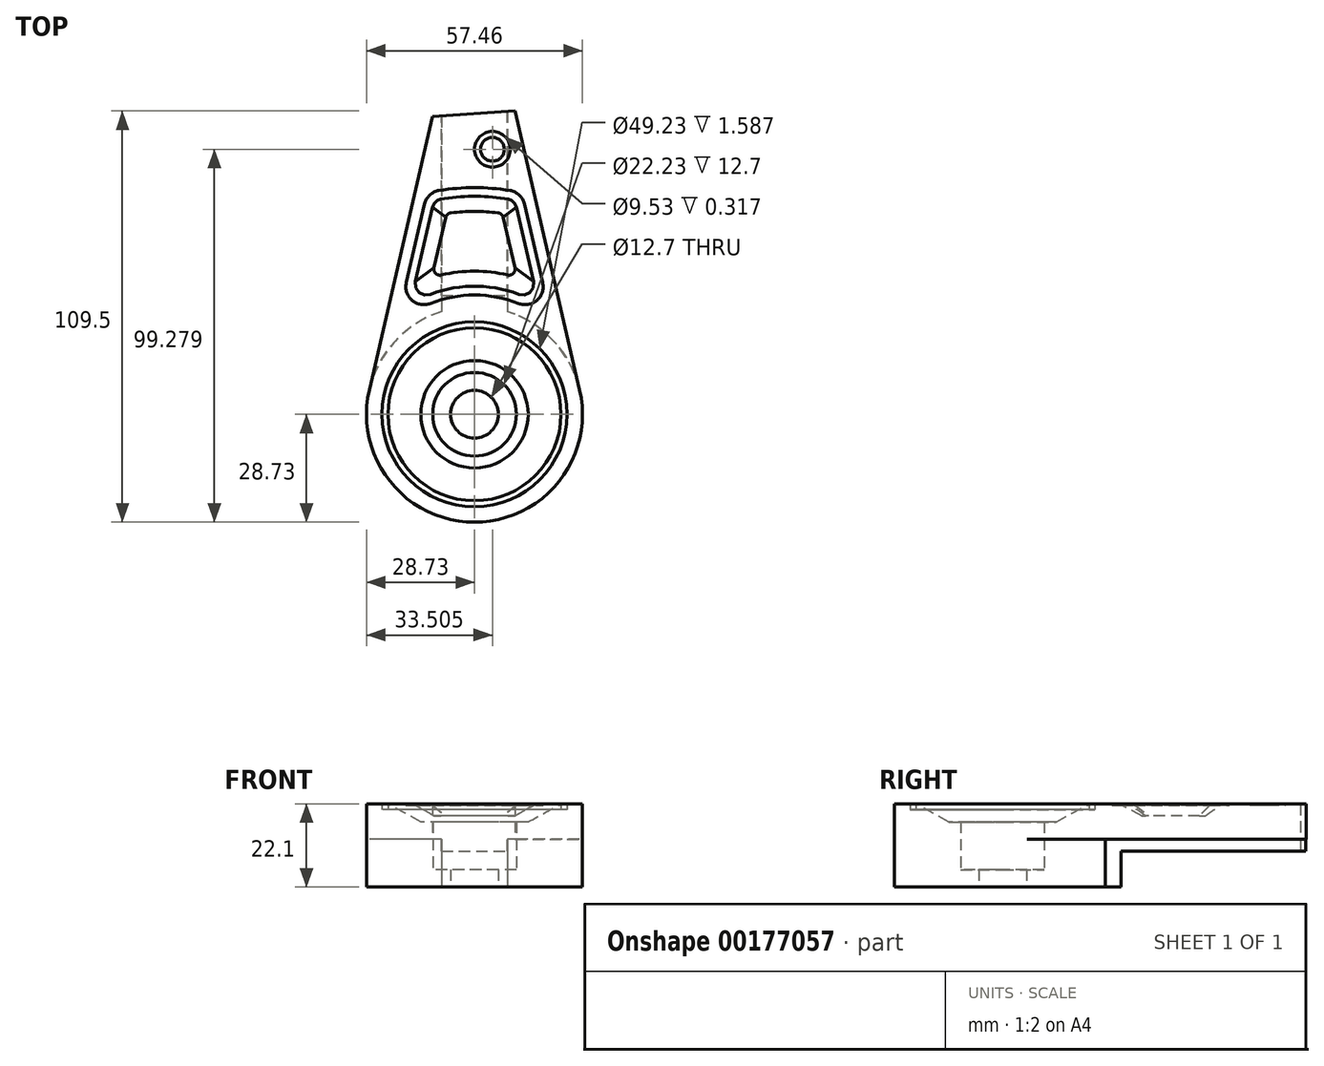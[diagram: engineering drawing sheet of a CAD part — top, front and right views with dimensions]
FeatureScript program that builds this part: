
annotation { "Feature Type Name" : "Feature", "Feature Type Description" : "" }
export const myFeature = defineFeature(function(context is Context, id is Id, definition is map)
    precondition{}
    {
        {
            var Q0;
            Q0=qCreatedBy(makeId("Top.planeOp"),FACE);
            var sketch = newSketch(context, id + "F0", { "sketchPlane" : qUnion([Q0])});
            skArc(sketch, "E0", {"start": v(-8.74, 27.37) * mm, "mid": v(0, -28.73) * mm, "end": v(8.74, 27.37) * mm});
            skLineSegment(sketch, "E1.bottom", {"start": v(-8.74, 31.6) * mm, "end": v(8.74, 31.6) * mm});
            skLineSegment(sketch, "E1.left", {"start": v(-8.74, 31.6) * mm, "end": v(-8.74, 27.37) * mm});
            skLineSegment(sketch, "E1.right", {"start": v(8.74, 31.6) * mm, "end": v(8.74, 27.37) * mm});
            skSolve(sketch);
        }
        {
            var Q0;
            Q0 = qSketchRegion(id + "F0", true);
            extrude(context, id + "F1", {"entities" : qUnion([Q0]), "depth" : 12.7 * mm});
        }
        {
            var Q0;
            Q0=makeQuery(id+"F1.opExtrude","CAP_FACE",FACE,{"disambiguationData":[OSD([sQuery(id+"F0.wireOp",EDGE,"E0"),sQuery(id+"F0.wireOp",EDGE,"E1.bottom"),sQuery(id+"F0.wireOp",EDGE,"E1.left"),sQuery(id+"F0.wireOp",EDGE,"E1.right")])],"isStart":false});
            var sketch = newSketch(context, id + "F2", { "sketchPlane" : qUnion([Q0])});
            skArc(sketch, "E2", {"start": v(-28, 6.46) * mm, "mid": v(0, -28.73) * mm, "end": v(28, 6.46) * mm});
            skLineSegment(sketch, "E3", {"start": v(10.84, 80.77) * mm, "end": v(-11.2, 79.23) * mm});
            skPoint(sketch, "E4.orphan", {"position": v(-37.72, -35.67) * mm});
            skPoint(sketch, "E5.orphan", {"position": v(37.72, -35.67) * mm});
            skLineSegment(sketch, "E6.trimOffspring", {"start": v(-11.2, 79.23) * mm, "end": v(-28, 6.46) * mm});
            skLineSegment(sketch, "E7.trimOffspring", {"start": v(10.84, 80.77) * mm, "end": v(28, 6.46) * mm});
            skPoint(sketch, "E8.MirrorCS.start.orphan", {"position": v(-27.86, 248.39) * mm});
            skPoint(sketch, "E9.start.orphan", {"position": v(27.86, 248.39) * mm});
            skSolve(sketch);
        }
        {
            var Q0;
            Q0 = qSketchRegion(id + "F2", true);
            extrude(context, id + "F3", {"entities" : qUnion([Q0]), "operationType" : NewBodyOperationType.ADD, "depth" : 9.4 * mm});
        }
        {
            var Q0;
            Q0=makeQuery(id+"F3.opExtrude","CAP_FACE",FACE,{"disambiguationData":[OSD([sQuery(id+"F2.wireOp",EDGE,"E2"),sQuery(id+"F2.wireOp",EDGE,"E3"),sQuery(id+"F2.wireOp",EDGE,"E6.trimOffspring"),sQuery(id+"F2.wireOp",EDGE,"E7.trimOffspring")])],"isStart":true});
            var sketch = newSketch(context, id + "F4", { "sketchPlane" : qUnion([Q0])});
            skLineSegment(sketch, "E10.bottom", {"start": v(8.74, -31.6) * mm, "end": v(-8.74, -31.6) * mm});
            skLineSegment(sketch, "E10.left", {"start": v(8.74, -31.6) * mm, "end": v(8.74, -80.63) * mm});
            skLineSegment(sketch, "E10.right", {"start": v(-8.74, -31.6) * mm, "end": v(-8.74, -79.4) * mm});
            skLineSegment(sketch, "E11", {"start": v(8.74, -80.63) * mm, "end": v(-8.74, -79.4) * mm});
            skSolve(sketch);
        }
        {
            var Q0;
            Q0=makeQuery(id+"F4.imprint","IMPRINT",FACE,{"disambiguationData":[TD([[makeQuery(id+"F4.imprint","IMPRINT",EDGE,{"derivedFrom":sQuery(id+"F4.wireOp",EDGE,"E10.bottom")}),-1.0]])]});
            var Q1;
            Q1 = qConstructionFilter(qBodyType(qCreatedBy(id + "F4" ,EDGE), BodyType.WIRE), ConstructionObject.NO);
            extrude(context, id + "F5", {"entities" : qUnion([Q0]), "operationType" : NewBodyOperationType.ADD, "surfaceEntities" : qUnion([Q1]), "depth" : 3.17 * mm});
        }
        {
            var Q0;
            Q0=makeQuery(id+"F3.opExtrude","CAP_FACE",FACE,{"disambiguationData":[OSD([sQuery(id+"F2.wireOp",EDGE,"E2"),sQuery(id+"F2.wireOp",EDGE,"E3"),sQuery(id+"F2.wireOp",EDGE,"E6.trimOffspring"),sQuery(id+"F2.wireOp",EDGE,"E7.trimOffspring")])],"isStart":false});
            var sketch = newSketch(context, id + "F6", { "sketchPlane" : qUnion([Q0])});
            skCircle(sketch, "E12", {"center": v(0, 0) * mm, "radius": 24.61 * mm});
            skCircle(sketch, "E13", {"center": v(0, 0) * mm, "radius": 23.03 * mm});
            skSolve(sketch);
        }
        {
            var Q0;
            Q0 = qSketchRegion(id + "F6", true);
            extrude(context, id + "F7", {"entities" : qUnion([Q0]), "endBound" : BoundingType.SYMMETRIC, "depth" : 3.17 * mm});
        }
        {
            var Q0;
            Q0=makeQuery(id+"F7.opExtrude","SWEPT_BODY",BODY,{"disambiguationData":[OSD([sQuery(id+"F6.wireOp",EDGE,"E12"),sQuery(id+"F6.wireOp",EDGE,"E13")])]});
            var Q1;
            Q1=makeQuery(id+"F1.opExtrude","SWEPT_BODY",BODY,{"disambiguationData":[OSD([sQuery(id+"F0.wireOp",EDGE,"E0"),sQuery(id+"F0.wireOp",EDGE,"E1.bottom"),sQuery(id+"F0.wireOp",EDGE,"E1.left"),sQuery(id+"F0.wireOp",EDGE,"E1.right")])]});
            booleanBodies(context, id + "F8", {"operationType" : BooleanOperationType.SUBTRACTION, "tools" : qUnion([Q0]), "targets" : qUnion([Q1])});
        }
        {
            var Q0;
            Q0=qCreatedBy(makeId("Front.planeOp"),FACE);
            var sketch = newSketch(context, id + "F9", { "sketchPlane" : qUnion([Q0])});
            skLineSegment(sketch, "E14.bottom", {"start": v(0, 22.1) * mm, "end": v(14.29, 22.1) * mm});
            skLineSegment(sketch, "E14.top", {"start": v(0, 17.32) * mm, "end": v(14.29, 17.32) * mm});
            skLineSegment(sketch, "E14.left", {"start": v(0, 22.1) * mm, "end": v(0, 17.32) * mm});
            skLineSegment(sketch, "E15.bottom", {"start": v(0, 22.1) * mm, "end": v(23.03, 22.1) * mm});
            skLineSegment(sketch, "E15.left", {"start": v(0, 22.1) * mm, "end": v(0, 15.75) * mm});
            skLineSegment(sketch, "E16", {"start": v(23.03, 22.1) * mm, "end": v(14.29, 17.32) * mm});
            skSolve(sketch);
        }
        {
            var Q0;
            Q0 = qSketchRegion(id + "F9", true);
            var Q1;
            Q1=sQuery(id+"F9.wireOp",EDGE,"E15.left");
            revolve(context, id + "F10", {"entities" : qUnion([Q0]), "axis" : qUnion([Q1]), "revolveType" : RevolveType.FULL});
        }
        {
            var Q0;
            Q0=makeQuery(id+"F10.opRevolve","SWEPT_BODY",BODY,{"disambiguationData":[OSD([sQuery(id+"F9.wireOp",EDGE,"E14.top"),sQuery(id+"F9.wireOp",EDGE,"E15.bottom"),sQuery(id+"F9.wireOp",EDGE,"E15.left"),sQuery(id+"F9.wireOp",EDGE,"E16")])]});
            var Q1;
            Q1=makeQuery(id+"F1.opExtrude","SWEPT_BODY",BODY,{"disambiguationData":[OSD([sQuery(id+"F0.wireOp",EDGE,"E0"),sQuery(id+"F0.wireOp",EDGE,"E1.bottom"),sQuery(id+"F0.wireOp",EDGE,"E1.left"),sQuery(id+"F0.wireOp",EDGE,"E1.right")])]});
            booleanBodies(context, id + "F11", {"operationType" : BooleanOperationType.SUBTRACTION, "tools" : qUnion([Q0]), "targets" : qUnion([Q1])});
        }
        {
            var Q0;
            Q0=makeQuery(id+"F11.opBoolean","COPY",FACE,{"derivedFrom":makeQuery(id+"F10.opRevolve","SWEPT_FACE",FACE,{"disambiguationData":[OSD([sQuery(id+"F9.wireOp",EDGE,"E14.top")])]})});
            var sketch = newSketch(context, id + "F12", { "sketchPlane" : qUnion([Q0])});
            skCircle(sketch, "E17", {"center": v(0, 0) * mm, "radius": 11.11 * mm});
            skSolve(sketch);
        }
        {
            var Q0;
            Q0=makeQuery(id+"F12.imprint","IMPRINT",FACE,{"disambiguationData":[TD([[makeQuery(id+"F12.imprint","IMPRINT",EDGE,{"derivedFrom":sQuery(id+"F12.wireOp",EDGE,"E17")}),1.0]])]});
            extrude(context, id + "F13", {"entities" : qUnion([Q0]), "endBound" : BoundingType.SYMMETRIC, "depth" : 25.4 * mm});
        }
        {
            var Q0;
            Q0=makeQuery(id+"F13.opExtrude","SWEPT_BODY",BODY,{"disambiguationData":[OSD([sQuery(id+"F12.wireOp",EDGE,"E17")])]});
            var Q1;
            Q1=makeQuery(id+"F1.opExtrude","SWEPT_BODY",BODY,{"disambiguationData":[OSD([sQuery(id+"F0.wireOp",EDGE,"E0"),sQuery(id+"F0.wireOp",EDGE,"E1.bottom"),sQuery(id+"F0.wireOp",EDGE,"E1.left"),sQuery(id+"F0.wireOp",EDGE,"E1.right")])]});
            booleanBodies(context, id + "F14", {"operationType" : BooleanOperationType.SUBTRACTION, "tools" : qUnion([Q0]), "targets" : qUnion([Q1])});
        }
        {
            var Q0;
            {var subQ0=sQuery(id+"F2.wireOp",EDGE,"E6.trimOffspring");var subQ1=sQuery(id+"F2.wireOp",EDGE,"E3");var subQ2=sQuery(id+"F2.wireOp",EDGE,"E2");var subQ3=sQuery(id+"F2.wireOp",EDGE,"E7.trimOffspring");Q0=makeQuery(id+"F8.opBoolean","SPLIT",FACE,{"disambiguationData":[TD([makeQuery(id+"F1.opExtrude","SWEPT_FACE",FACE,{"disambiguationData":[OSD([sQuery(id+"F0.wireOp",EDGE,"E0")])]})])],"derivedFrom":makeQuery(id+"F3.opExtrude","CAP_FACE",FACE,{"disambiguationData":[OSD([subQ2,subQ1,subQ0,subQ3])],"isStart":false})});}
            var sketch = newSketch(context, id + "F15", { "sketchPlane" : qUnion([Q0])});
            skCircle(sketch, "E18", {"center": v(4.78, 70.55) * mm, "radius": 4.76 * mm});
            skCircle(sketch, "E19", {"center": v(4.78, 70.55) * mm, "radius": 3.18 * mm});
            skSolve(sketch);
        }
        {
            var Q0;
            Q0 = qSketchRegion(id + "F15", true);
            extrude(context, id + "F16", {"entities" : qUnion([Q0]), "endBound" : BoundingType.SYMMETRIC, "depth" : 0.64 * mm});
        }
        {
            var Q0;
            Q0=makeQuery(id+"F16.opExtrude","SWEPT_BODY",BODY,{"disambiguationData":[OSD([sQuery(id+"F15.wireOp",EDGE,"E18"),sQuery(id+"F15.wireOp",EDGE,"E19")])]});
            var Q1;
            Q1=makeQuery(id+"F1.opExtrude","SWEPT_BODY",BODY,{"disambiguationData":[OSD([sQuery(id+"F0.wireOp",EDGE,"E0"),sQuery(id+"F0.wireOp",EDGE,"E1.bottom"),sQuery(id+"F0.wireOp",EDGE,"E1.left"),sQuery(id+"F0.wireOp",EDGE,"E1.right")])]});
            booleanBodies(context, id + "F17", {"operationType" : BooleanOperationType.SUBTRACTION, "tools" : qUnion([Q0]), "targets" : qUnion([Q1])});
        }
        {
            var Q0;
            {var subQ0=sQuery(id+"F2.wireOp",EDGE,"E6.trimOffspring");var subQ2=sQuery(id+"F2.wireOp",EDGE,"E3");var subQ4=sQuery(id+"F2.wireOp",EDGE,"E2");var subQ6=makeQuery(id+"F1.opExtrude","SWEPT_FACE",FACE,{"disambiguationData":[OSD([sQuery(id+"F0.wireOp",EDGE,"E0")])]});var subQ7=sQuery(id+"F2.wireOp",EDGE,"E7.trimOffspring");Q0=makeQuery(id+"F17.opBoolean","SPLIT",FACE,{"disambiguationData":[TD([subQ6])],"derivedFrom":makeQuery(id+"F8.opBoolean","SPLIT",FACE,{"disambiguationData":[TD([subQ6])],"derivedFrom":makeQuery(id+"F3.opExtrude","CAP_FACE",FACE,{"disambiguationData":[OSD([subQ4,subQ2,subQ0,subQ7])],"isStart":false})})});}
            var sketch = newSketch(context, id + "F18", { "sketchPlane" : qUnion([Q0])});
            skArc(sketch, "E20", {"start": v(9.36, 59.6) * mm, "mid": v(0, 60.33) * mm, "end": v(-9.36, 59.6) * mm});
            skArc(sketch, "E21", {"start": v(11.72, 29.5) * mm, "mid": v(0, 31.75) * mm, "end": v(-11.72, 29.5) * mm});
            skLineSegment(sketch, "E22", {"start": v(18.14, 35.02) * mm, "end": v(13.32, 55.91) * mm});
            skLineSegment(sketch, "E23.MirrorCS", {"start": v(-18.14, 35.02) * mm, "end": v(-13.32, 55.91) * mm});
            skPoint(sketch, "E24.visualSharp", {"position": v(-11.28, 57.66) * mm});
            skPoint(sketch, "E25.visualSharp", {"position": v(11.28, 57.66) * mm});
            skPoint(sketch, "E26.visualSharp", {"position": v(-12.6, 59) * mm});
            skArc(sketch, "E26.filletArc", {"start": v(-9.36, 59.6) * mm, "mid": v(-11.9, 58.36) * mm, "end": v(-13.32, 55.91) * mm});
            skPoint(sketch, "E27.visualSharp", {"position": v(12.6, 59) * mm});
            skArc(sketch, "E27.filletArc", {"start": v(13.32, 55.91) * mm, "mid": v(11.9, 58.36) * mm, "end": v(9.36, 59.6) * mm});
            skPoint(sketch, "E28.visualSharp", {"position": v(-18.13, 27.99) * mm});
            skPoint(sketch, "E29.visualSharp", {"position": v(18.13, 27.99) * mm});
            skPoint(sketch, "E30.visualSharp", {"position": v(-20.66, 24.11) * mm});
            skArc(sketch, "E30.filletArc", {"start": v(-18.14, 35.02) * mm, "mid": v(-16.6, 30.32) * mm, "end": v(-11.72, 29.5) * mm});
            skPoint(sketch, "E31.visualSharp", {"position": v(20.66, 24.11) * mm});
            skArc(sketch, "E31.filletArc", {"start": v(11.72, 29.5) * mm, "mid": v(16.6, 30.32) * mm, "end": v(18.14, 35.02) * mm});
            skSolve(sketch);
        }
        {
            var Q0;
            Q0 = qSketchRegion(id + "F18", true);
            extrude(context, id + "F19", {"entities" : qUnion([Q0]), "endBound" : BoundingType.SYMMETRIC, "depth" : 0.76 * mm});
        }
        {
            var Q0;
            Q0=makeQuery(id+"F19.opExtrude","SWEPT_BODY",BODY,{"disambiguationData":[OSD([sQuery(id+"F18.wireOp",EDGE,"E20"),sQuery(id+"F18.wireOp",EDGE,"QQfPZb6T-z4vG-od9X-flIt-BDM9YzBF81dE"),sQuery(id+"F18.wireOp",EDGE,"E21"),sQuery(id+"F18.wireOp",EDGE,"x9Glj3Va-BeVH-0q31-jCwU-7eNUVLCWfRpr"),sQuery(id+"F18.wireOp",EDGE,"E22"),sQuery(id+"F18.wireOp",EDGE,"5VmBpSvH-0JUU-8XrI-SHU1-adJSwn0DBkaH"),sQuery(id+"F18.wireOp",EDGE,"E23.MirrorCS"),sQuery(id+"F18.wireOp",EDGE,"3f89a360-dbe8-4113-bc30-97e3e043b985.trimOffspring"),sQuery(id+"F18.wireOp",EDGE,"E24.filletArc"),sQuery(id+"F18.wireOp",EDGE,"E25.filletArc"),sQuery(id+"F18.wireOp",EDGE,"E26.filletArc"),sQuery(id+"F18.wireOp",EDGE,"E27.filletArc"),sQuery(id+"F18.wireOp",EDGE,"E28.filletArc"),sQuery(id+"F18.wireOp",EDGE,"E29.filletArc"),sQuery(id+"F18.wireOp",EDGE,"E30.filletArc"),sQuery(id+"F18.wireOp",EDGE,"E31.filletArc")])]});
            var Q1;
            Q1=makeQuery(id+"F1.opExtrude","SWEPT_BODY",BODY,{"disambiguationData":[OSD([sQuery(id+"F0.wireOp",EDGE,"E0"),sQuery(id+"F0.wireOp",EDGE,"E1.bottom"),sQuery(id+"F0.wireOp",EDGE,"E1.left"),sQuery(id+"F0.wireOp",EDGE,"E1.right")])]});
            booleanBodies(context, id + "F20", {"operationType" : BooleanOperationType.SUBTRACTION, "tools" : qUnion([Q0]), "targets" : qUnion([Q1])});
        }
        {
            var Q0;
            {var subQ0=sQuery(id+"F2.wireOp",EDGE,"E6.trimOffspring");var subQ2=sQuery(id+"F2.wireOp",EDGE,"E3");var subQ4=sQuery(id+"F2.wireOp",EDGE,"E2");var subQ6=makeQuery(id+"F1.opExtrude","SWEPT_FACE",FACE,{"disambiguationData":[OSD([sQuery(id+"F0.wireOp",EDGE,"E0")])]});var subQ7=sQuery(id+"F2.wireOp",EDGE,"E7.trimOffspring");Q0=makeQuery(id+"F17.opBoolean","SPLIT",FACE,{"disambiguationData":[TD([subQ6])],"derivedFrom":makeQuery(id+"F8.opBoolean","SPLIT",FACE,{"disambiguationData":[TD([subQ6])],"derivedFrom":makeQuery(id+"F3.opExtrude","CAP_FACE",FACE,{"disambiguationData":[OSD([subQ4,subQ2,subQ0,subQ7])],"isStart":false})})});}
            var sketch = newSketch(context, id + "F21", { "sketchPlane" : qUnion([Q0])});
            skLineSegment(sketch, "E32", {"start": v(10.74, 38.95) * mm, "end": v(7.63, 52.42) * mm});
            skArc(sketch, "E33", {"start": v(8.84, 37.06) * mm, "mid": v(0, 38.1) * mm, "end": v(-8.84, 37.06) * mm});
            skArc(sketch, "E34", {"start": v(6.28, 53.63) * mm, "mid": v(0, 54) * mm, "end": v(-6.28, 53.63) * mm});
            skLineSegment(sketch, "E35", {"start": v(-7.63, 52.42) * mm, "end": v(-10.74, 38.95) * mm});
            skPoint(sketch, "E36.visualSharp", {"position": v(-11.34, 36.37) * mm});
            skArc(sketch, "E36.filletArc", {"start": v(-10.74, 38.95) * mm, "mid": v(-10.32, 37.47) * mm, "end": v(-8.84, 37.06) * mm});
            skPoint(sketch, "E37.visualSharp", {"position": v(11.34, 36.37) * mm});
            skArc(sketch, "E37.filletArc", {"start": v(8.84, 37.06) * mm, "mid": v(10.32, 37.47) * mm, "end": v(10.74, 38.95) * mm});
            skPoint(sketch, "E38.visualSharp", {"position": v(7.38, 53.5) * mm});
            skArc(sketch, "E38.filletArc", {"start": v(7.63, 52.42) * mm, "mid": v(7.15, 53.24) * mm, "end": v(6.28, 53.63) * mm});
            skPoint(sketch, "E39.visualSharp", {"position": v(-7.38, 53.5) * mm});
            skArc(sketch, "E39.filletArc", {"start": v(-6.28, 53.63) * mm, "mid": v(-7.15, 53.24) * mm, "end": v(-7.63, 52.42) * mm});
            skSolve(sketch);
        }
        {
            var Q0;
            Q0=qCreatedBy(makeId("Top.planeOp"),FACE);
            cPlane(context, id + "F22", {"entities" : qUnion([Q0]), "cplaneType" : CPlaneType.OFFSET, "offset" : 25.4 * mm, "width" : 152.4 * mm, "height" : 152.4 * mm});
        }
        {
            var Q0;
            Q0=qCreatedBy(id+"F22.planeOp",FACE);
            var sketch = newSketch(context, id + "F23", { "sketchPlane" : qUnion([Q0])});
            skArc(sketch, "E40", {"start": v(9.17, 58.03) * mm, "mid": v(0, 58.75) * mm, "end": v(-9.17, 58.03) * mm});
            skArc(sketch, "E41", {"start": v(12.34, 30.98) * mm, "mid": v(0, 33.35) * mm, "end": v(-12.34, 30.98) * mm});
            skLineSegment(sketch, "E42", {"start": v(-16.6, 34.65) * mm, "end": v(-11.77, 55.6) * mm});
            skLineSegment(sketch, "E43", {"start": v(16.6, 34.65) * mm, "end": v(11.77, 55.6) * mm});
            skPoint(sketch, "E44.visualSharp", {"position": v(-11.3, 57.65) * mm});
            skArc(sketch, "E44.filletArc", {"start": v(-9.17, 58.03) * mm, "mid": v(-10.84, 57.22) * mm, "end": v(-11.77, 55.6) * mm});
            skPoint(sketch, "E45.visualSharp", {"position": v(-18.15, 27.98) * mm});
            skArc(sketch, "E45.filletArc", {"start": v(-16.6, 34.65) * mm, "mid": v(-15.58, 31.52) * mm, "end": v(-12.34, 30.98) * mm});
            skPoint(sketch, "E46.visualSharp", {"position": v(18.15, 27.98) * mm});
            skArc(sketch, "E46.filletArc", {"start": v(12.34, 30.98) * mm, "mid": v(15.58, 31.52) * mm, "end": v(16.6, 34.65) * mm});
            skPoint(sketch, "E47.visualSharp", {"position": v(11.3, 57.65) * mm});
            skArc(sketch, "E47.filletArc", {"start": v(11.77, 55.6) * mm, "mid": v(10.84, 57.22) * mm, "end": v(9.17, 58.03) * mm});
            skSolve(sketch);
        }
        {
            var Q0;
            Q0=makeQuery(id+"F1.opExtrude","CAP_FACE",FACE,{"disambiguationData":[OSD([sQuery(id+"F0.wireOp",EDGE,"E0"),sQuery(id+"F0.wireOp",EDGE,"E1.bottom"),sQuery(id+"F0.wireOp",EDGE,"E1.left"),sQuery(id+"F0.wireOp",EDGE,"E1.right")])],"isStart":true});
            var sketch = newSketch(context, id + "F24", { "sketchPlane" : qUnion([Q0])});
            skPoint(sketch, "E48", {"position": v(0, 0) * mm});
            skSolve(sketch);
        }
        {
            var Q0;
            Q0=sQuery(id+"F24.wireOp",VERTEX,"E48");
            var Q1;
            Q1=makeQuery(id+"F1.opExtrude","SWEPT_BODY",BODY,{"disambiguationData":[OSD([sQuery(id+"F0.wireOp",EDGE,"E0"),sQuery(id+"F0.wireOp",EDGE,"E1.bottom"),sQuery(id+"F0.wireOp",EDGE,"E1.left"),sQuery(id+"F0.wireOp",EDGE,"E1.right")])]});
            hole(context, id + "F25", {"style" : HoleStyle.SIMPLE, "endStyle" : HoleEndStyle.THROUGH, "holeDiameter" : 12.7 * mm, "startFromSketch" : true, "locations" : qUnion([Q0]), "scope" : qUnion([Q1]), "isTappedThrough" : true});
        }
        {
            var Q0;
            Q0=makeQuery(id+"F23.imprint","IMPRINT",FACE,{"disambiguationData":[TD([[makeQuery(id+"F23.imprint","IMPRINT",EDGE,{"derivedFrom":sQuery(id+"F23.wireOp",EDGE,"E40")}),1.0]])]});
            var Q1;
            Q1=makeQuery(id+"F21.imprint","IMPRINT",FACE,{"disambiguationData":[TD([[makeQuery(id+"F21.imprint","IMPRINT",EDGE,{"derivedFrom":sQuery(id+"F21.wireOp",EDGE,"E32")}),1.0]])]});
            loft(context, id + "F26", {"sheetProfilesArray" : [{ "sheetProfileEntities" : qUnion([Q0]) }, { "sheetProfileEntities" : qUnion([Q1]) }]});
        }
        {
            var Q0;
            Q0=makeQuery(id+"F26.opLoft","SWEPT_BODY",BODY,{"disambiguationData":[OSD([makeQuery(id+"F21.imprint","IMPRINT",FACE,{"disambiguationData":[TD([[makeQuery(id+"F21.imprint","IMPRINT",EDGE,{"derivedFrom":sQuery(id+"F21.wireOp",EDGE,"E32")}),1.0]])]}),makeQuery(id+"F23.imprint","IMPRINT",FACE,{"disambiguationData":[TD([[makeQuery(id+"F23.imprint","IMPRINT",EDGE,{"derivedFrom":sQuery(id+"F23.wireOp",EDGE,"E40")}),1.0]])]})])]});
            transform(context, id + "F27", {"entities" : qUnion([Q0]), "transformType" : TransformType.TRANSLATION_3D, "dx" : 0 * mm, "dy" : 0 * mm, "dz" : -3.17 * mm, "makeCopy" : false});
        }
        {
            var Q0;
            Q0=makeQuery(id+"F26.opLoft","SWEPT_BODY",BODY,{"disambiguationData":[OSD([makeQuery(id+"F21.imprint","IMPRINT",FACE,{"disambiguationData":[TD([[makeQuery(id+"F21.imprint","IMPRINT",EDGE,{"derivedFrom":sQuery(id+"F21.wireOp",EDGE,"E32")}),1.0]])]}),makeQuery(id+"F23.imprint","IMPRINT",FACE,{"disambiguationData":[TD([[makeQuery(id+"F23.imprint","IMPRINT",EDGE,{"derivedFrom":sQuery(id+"F23.wireOp",EDGE,"E40")}),1.0]])]})])]});
            var Q1;
            Q1=makeQuery(id+"F1.opExtrude","SWEPT_BODY",BODY,{"disambiguationData":[OSD([sQuery(id+"F0.wireOp",EDGE,"E0"),sQuery(id+"F0.wireOp",EDGE,"E1.bottom"),sQuery(id+"F0.wireOp",EDGE,"E1.left"),sQuery(id+"F0.wireOp",EDGE,"E1.right")])]});
            booleanBodies(context, id + "F28", {"operationType" : BooleanOperationType.SUBTRACTION, "tools" : qUnion([Q0]), "targets" : qUnion([Q1])});
        }
    });
